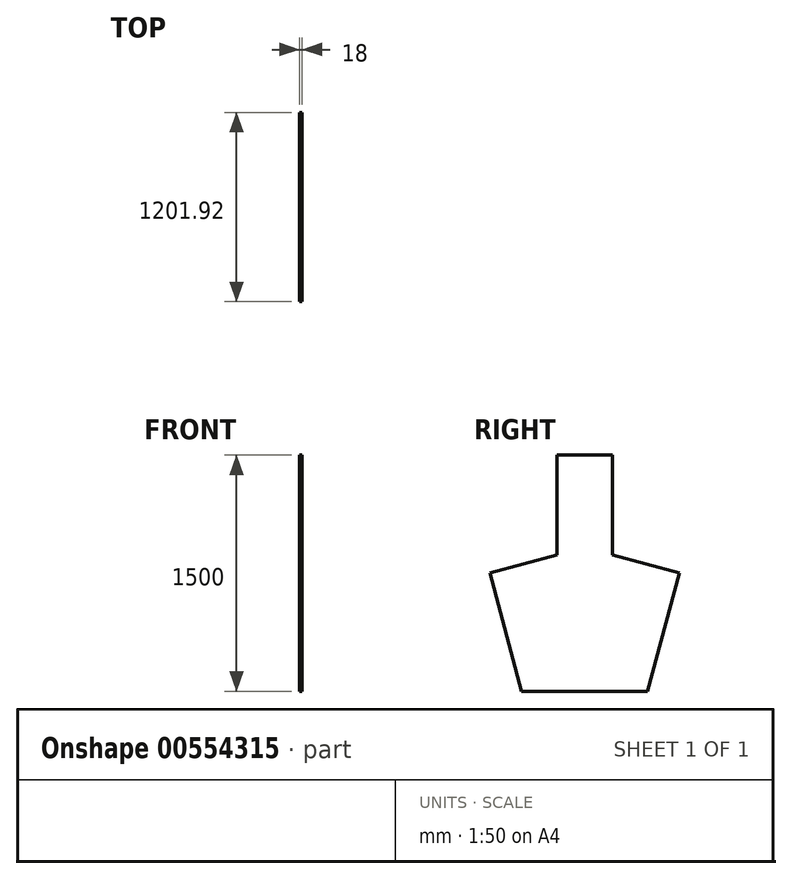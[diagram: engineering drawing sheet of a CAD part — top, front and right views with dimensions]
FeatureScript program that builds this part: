
annotation { "Feature Type Name" : "Feature", "Feature Type Description" : "" }
export const myFeature = defineFeature(function(context is Context, id is Id, definition is map)
    precondition{}
    {
        {
            var Q0;
            Q0=qCreatedBy(makeId("Right.planeOp"), FACE);
            var sketch = newSketch(context, id + "F0", { "sketchPlane" : qUnion([Q0])});
            skLineSegment(sketch, "E0", {"start": v(-400, 0) * mm, "end": v(400, 0) * mm});
            skLineSegment(sketch, "E1", {"start": v(400, 0) * mm, "end": v(600.96, 750) * mm});
            skLineSegment(sketch, "E2", {"start": v(600.96, 750) * mm, "end": v(175, 864.14) * mm});
            skLineSegment(sketch, "E3", {"start": v(-400, 0) * mm, "end": v(-600.96, 750) * mm});
            skLineSegment(sketch, "E4", {"start": v(-600.96, 750) * mm, "end": v(-175, 864.14) * mm});
            skLineSegment(sketch, "E5", {"start": v(0, -161.1) * mm, "end": v(0, 1396.06) * mm, "construction": true});
            skLineSegment(sketch, "E6", {"start": v(-175, 864.14) * mm, "end": v(-175, 1500) * mm});
            skLineSegment(sketch, "E7", {"start": v(-175, 1500) * mm, "end": v(175, 1500) * mm});
            skLineSegment(sketch, "E8", {"start": v(175, 1500) * mm, "end": v(175, 864.14) * mm});
            skSolve(sketch);
        }
        {
            var Q0;
            Q0 = qSketchRegion(id + "F0", true);
            extrude(context, id + "F1", {"entities" : qUnion([Q0]), "depth" : 18 * mm, "offsetDistance" : 25 * mm});
        }
    });
